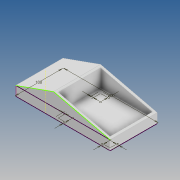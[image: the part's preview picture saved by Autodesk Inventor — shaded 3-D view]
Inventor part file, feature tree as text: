
AUTODESK INVENTOR PART (.ipt)
format: ipt  version: 2020 (Build 240168000, 168)  size: 117,760 bytes
history: native  units: mm
features: extrude x4, sketch x3
ambient origin geometry x8: Origin, YZ Plane, XZ Plane, XY Plane, X Axis, Y Axis, Z Axis, Center Point
bodies: Solid1 (feature_tree)
feature tree (7):
  extrude  "Extrusion1"  Depth=100.0mm
  extrude  "Extrusion2"  Depth=100.0mm TaperAngle=0.0deg
  sketch  "Sketch4"  dims[d23=5.0mm d24=5.0mm d25=5.0mm d26=5.0mm d27=5.0mm d28=5.0mm d29=68.75mm d30=0.0mm d31=10.0mm d32=0.0mm]
  extrude  "Extrusion3"  Depth=5.0mm
  extrude  "Extrusion4"  Depth=5.0mm
  sketch  "Sketch1"  dims[d0=200.0mm d1=100.0mm]
  sketch  "Sketch2"  dims[d2=20.0mm d3=0.0mm d10=100.0mm d11=0.0mm]
